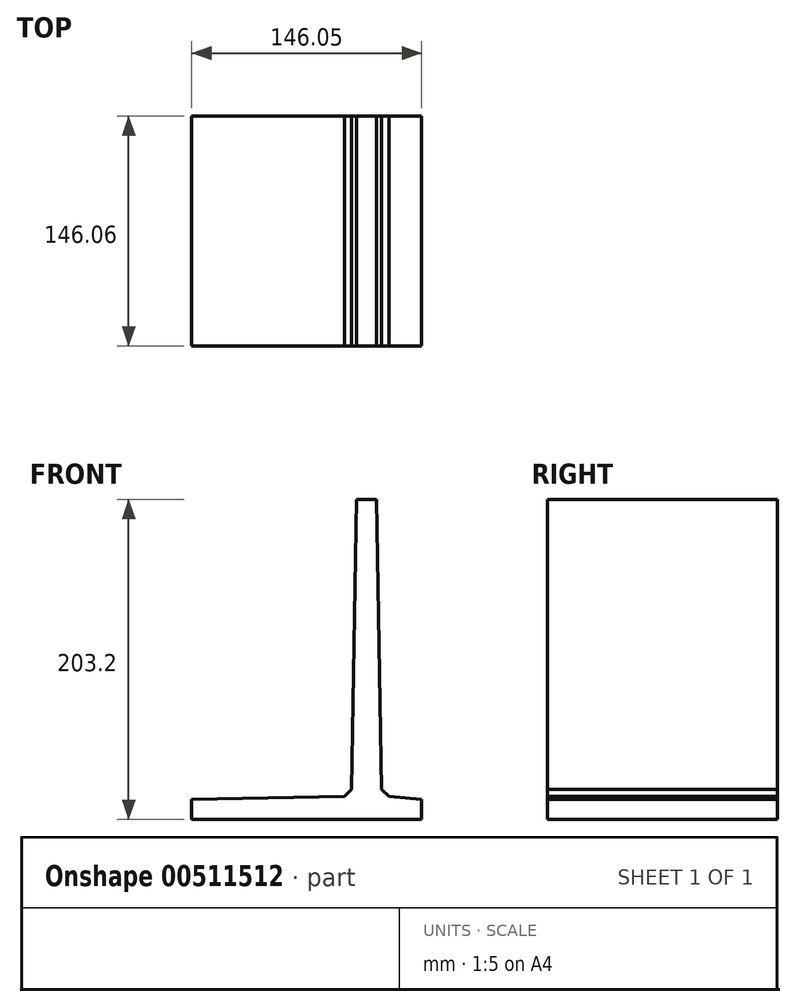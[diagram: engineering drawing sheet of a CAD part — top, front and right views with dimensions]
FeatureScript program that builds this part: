
annotation { "Feature Type Name" : "Feature", "Feature Type Description" : "" }
export const myFeature = defineFeature(function(context is Context, id is Id, definition is map)
    precondition{}
    {
        {
            var Q0;
            Q0=qCreatedBy(makeId("Front.planeOp"),FACE);
            var sketch = newSketch(context, id + "F0", { "sketchPlane" : qUnion([Q0])});
            skLineSegment(sketch, "E0", {"start": v(-6.35, 203.2) * mm, "end": v(6.35, 203.2) * mm});
            skLineSegment(sketch, "E1", {"start": v(6.35, 203.2) * mm, "end": v(9.53, 19.05) * mm});
            skLineSegment(sketch, "E2", {"start": v(9.52, 19.05) * mm, "end": v(14.1, 14.48) * mm});
            skLineSegment(sketch, "E3", {"start": v(34.93, 12.7) * mm, "end": v(34.93, 0) * mm});
            skLineSegment(sketch, "E4", {"start": v(34.93, 0) * mm, "end": v(-111.13, 0) * mm});
            skLineSegment(sketch, "E5", {"start": v(-111.13, 0) * mm, "end": v(-111.13, 12.7) * mm});
            skLineSegment(sketch, "E6", {"start": v(-111.13, 12.7) * mm, "end": v(-14.1, 14.48) * mm});
            skLineSegment(sketch, "E7", {"start": v(-14.1, 14.48) * mm, "end": v(-9.52, 19.05) * mm});
            skLineSegment(sketch, "E8", {"start": v(-9.52, 19.05) * mm, "end": v(-6.35, 203.2) * mm});
            skLineSegment(sketch, "E9", {"start": v(14.1, 14.48) * mm, "end": v(34.92, 12.7) * mm});
            skSolve(sketch);
        }
        {
            var Q0;
            Q0 = qSketchRegion(id + "F0", true);
            extrude(context, id + "F1", {"entities" : qUnion([Q0]), "endBound" : BoundingType.SYMMETRIC, "depth" : 146.05 * mm, "offsetDistance" : 25.4 * mm});
        }
    });
